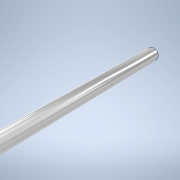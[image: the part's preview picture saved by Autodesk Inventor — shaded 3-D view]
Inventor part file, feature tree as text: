
AUTODESK INVENTOR PART (.ipt)
format: ipt  version: 2020.3 (Build 243373000, 373)  size: 96,768 bytes
history: native  units: mm
features: other x1, extrude x1, sketch x1
ambient origin geometry x8: Origin, YZ Plane, XZ Plane, XY Plane, X Axis, Y Axis, Z Axis, Center Point
bodies: Body1 (feature_tree)
feature tree (3):
  other  "ソリッド1"
  extrude  "押し出し1"  Depth=4.0mm
  sketch  "スケッチ1"
